# Revit family: BoilingWater_UnderBenchUnit_Rheem_On-TapAzure
name_source: partatom
category: Plumbing Fixtures
revit_build: Autodesk Revit Structure 2014 (Build: 20130308_1515(x64)
units: mm (PartAtom-declared; Revit-internal decimal feet)

## types (1)
- Azure
    BoilingOutletDia = 10 mm  [stored 0.0328084 ft]
    BoilingWaterUnitLocation = Within 1m of the Rheem Tap
    Default Elevation = 1219 mm
    DrainHoleRad = 25 mm  [stored 0.082021 ft]
    FilteredOutletDia = 6 mm  [stored 0.019685 ft]
    Manufacturer = Rheem
    MaxWaterPressure = 1000kPa
    MinWaterPressure = 100kPa
    ModifiedIssue_ANZRS = 151224.01 $
    OutletFor3/4"IDHose = 19 mm  [stored 0.062336 ft]
    PlumbingMaterial_ANZRS = Stainless Steel, Polished
    SupplyInletDia = 15 mm  [stored 0.0492126 ft]
    TapHole-SinkEdgeMax = 85 mm  [stored 0.278871 ft]
    URL = www.rheem.co.nz
    VentConnectionDia = 10 mm  [stored 0.0328084 ft]

note: [stored X ft] marks values corroborated as IEEE doubles in the binary element streams (Revit-internal decimal feet)

## geometry (parser evidence)
native form markers: Sweep x18
no freeform markers — native parametric forms only
